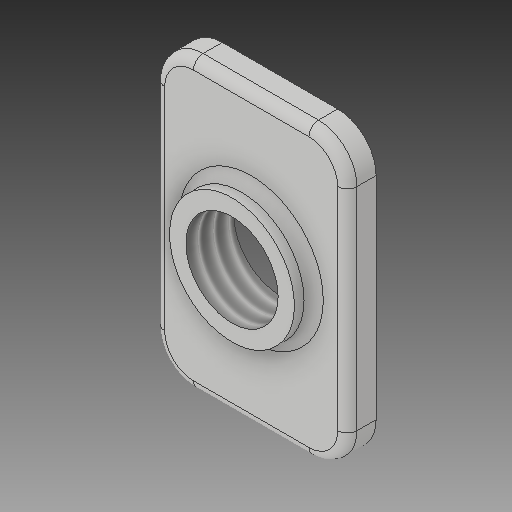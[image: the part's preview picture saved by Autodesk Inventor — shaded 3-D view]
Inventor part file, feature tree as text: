
AUTODESK INVENTOR PART (.ipt)
format: ipt  version: 2018 (Build 220112000, 112)  size: 176,128 bytes
history: native  units: mm
features: extrude x2, fillet x2, sketch x2, thread x1
ambient origin geometry x8: Origin, YZ Plane, XZ Plane, XY Plane, X Axis, Y Axis, Z Axis, Center Point
bodies: Solid1 (feature_tree)
feature tree (7):
  extrude  "Extrusion1"  Depth=15.0mm
  extrude  "Extrusion2"  Depth=2.0mm
  fillet  "Fillet1"  Radius=1.5mm
  thread  "Thread1"  [1 undecoded]
  fillet  "Fillet2"  Radius=1.0mm
  sketch  "Sketch1"  dims[d0=10.0mm d1=15.0mm]
  sketch  "Sketch2"  dims[d2=4.8mm d3=2.0mm d4=1.5mm d5=0.0mm d6=6.5mm d7=1.0mm d8=0.0mm d9=0.5mm d10=10.0mm d11=0.0mm d12=0.5mm]
note: 1 required parameter value undecoded (feature->parameter linkage not recoverable at this tier; creation-order binding heuristic only, values carry confidence <= 0.55)
